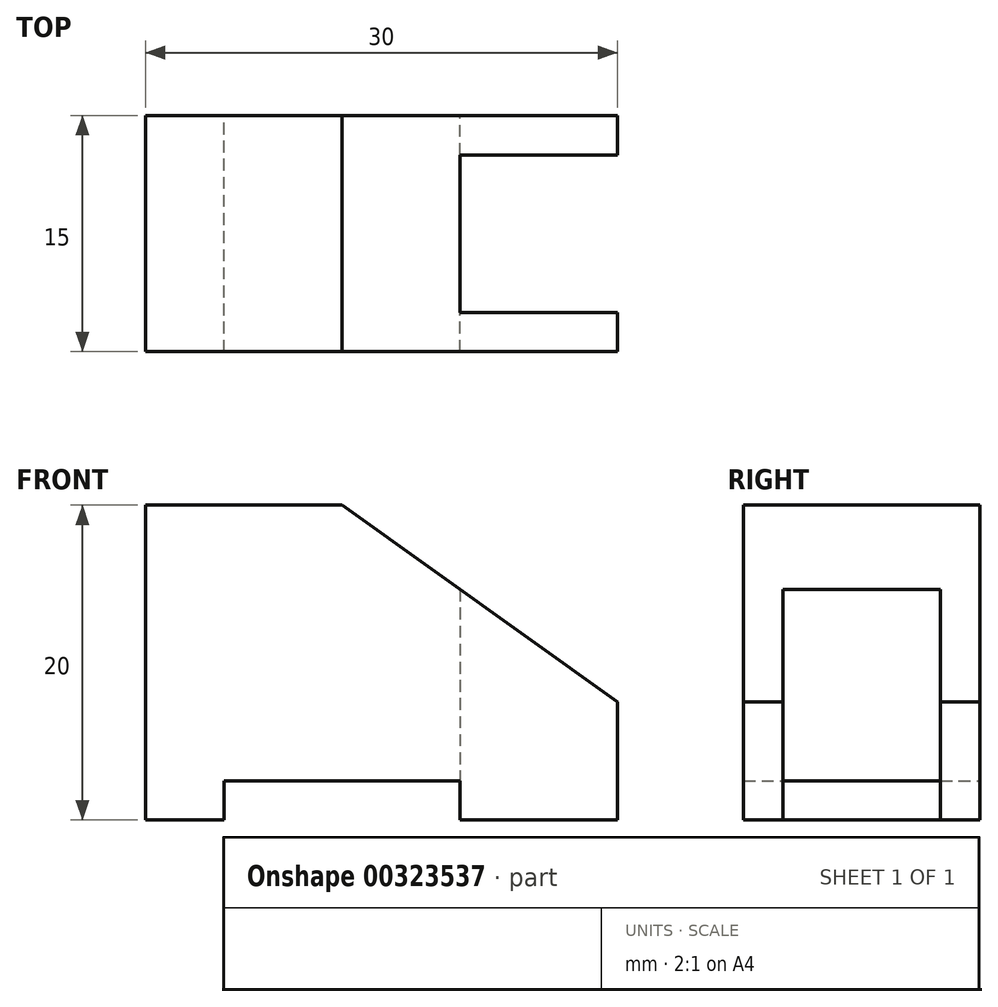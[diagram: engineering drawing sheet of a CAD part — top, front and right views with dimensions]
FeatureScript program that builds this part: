
annotation { "Feature Type Name" : "Feature", "Feature Type Description" : "" }
export const myFeature = defineFeature(function(context is Context, id is Id, definition is map)
    precondition{}
    {
        {
            var Q0;
            Q0=qCreatedBy(makeId("Front.planeOp"),FACE);
            var sketch = newSketch(context, id + "F0", { "sketchPlane" : qUnion([Q0])});
            skLineSegment(sketch, "E0", {"start": v(0, 0) * mm, "end": v(5, 0) * mm});
            skLineSegment(sketch, "E1", {"start": v(5, 0) * mm, "end": v(5, 2.5) * mm});
            skLineSegment(sketch, "E2", {"start": v(5, 2.5) * mm, "end": v(20, 2.5) * mm});
            skLineSegment(sketch, "E3", {"start": v(20, 2.5) * mm, "end": v(20, 0) * mm});
            skLineSegment(sketch, "E4", {"start": v(20, 0) * mm, "end": v(30, 0) * mm});
            skLineSegment(sketch, "E5", {"start": v(30, 0) * mm, "end": v(30, 7.5) * mm});
            skLineSegment(sketch, "E6", {"start": v(30, 7.5) * mm, "end": v(12.5, 20) * mm});
            skLineSegment(sketch, "E7", {"start": v(12.5, 20) * mm, "end": v(0, 20) * mm});
            skLineSegment(sketch, "E8", {"start": v(0, 20) * mm, "end": v(0, 0) * mm});
            skSolve(sketch);
        }
        {
            var Q0;
            Q0 = qSketchRegion(id + "F0", true);
            extrude(context, id + "F1", {"entities" : qUnion([Q0]), "endBound" : BoundingType.SYMMETRIC, "depth" : 15 * mm});
        }
        {
            var Q0;
            Q0=qCreatedBy(makeId("Top.planeOp"),FACE);
            var sketch = newSketch(context, id + "F2", { "sketchPlane" : qUnion([Q0])});
            skLineSegment(sketch, "E9", {"start": v(30, 5) * mm, "end": v(20, 5) * mm});
            skLineSegment(sketch, "E10", {"start": v(20, 5) * mm, "end": v(20, -5) * mm});
            skLineSegment(sketch, "E11", {"start": v(20, -5) * mm, "end": v(30, -5) * mm});
            skLineSegment(sketch, "E12", {"start": v(30, -5) * mm, "end": v(30, 5) * mm});
            skPoint(sketch, "E13.0", {"position": v(30, 0) * mm});
            skSolve(sketch);
        }
        {
            var Q0;
            Q0 = qSketchRegion(id + "F2", true);
            extrude(context, id + "F3", {"entities" : qUnion([Q0]), "operationType" : NewBodyOperationType.REMOVE, "endBound" : BoundingType.THROUGH_ALL, "depth" : 25 * mm});
        }
    });
